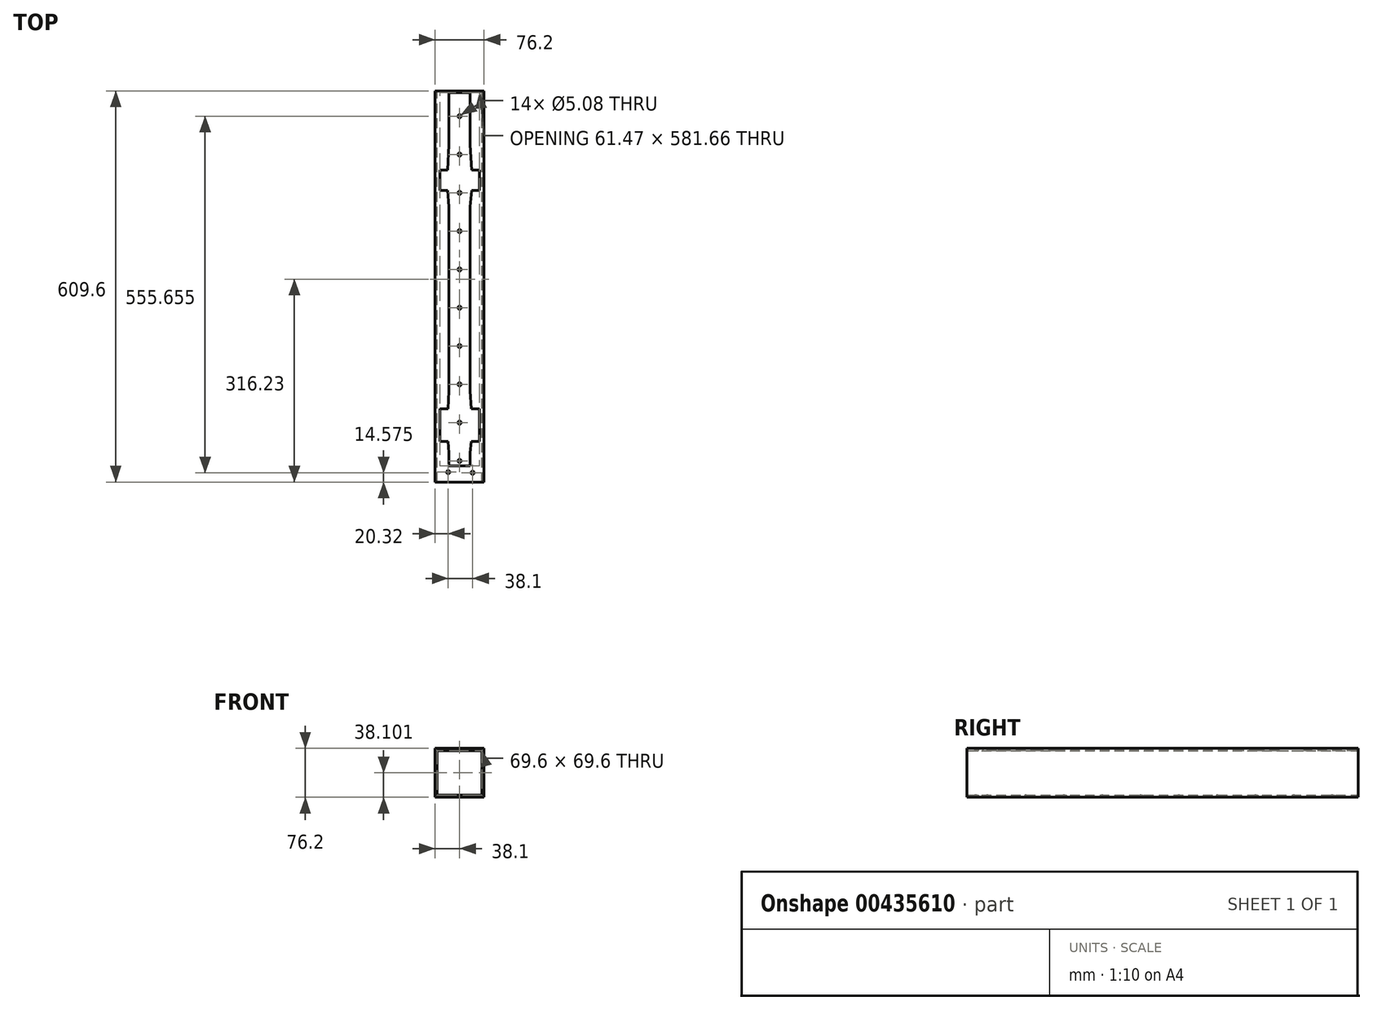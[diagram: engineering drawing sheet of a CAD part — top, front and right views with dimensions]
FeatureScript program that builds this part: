
annotation { "Feature Type Name" : "Feature", "Feature Type Description" : "" }
export const myFeature = defineFeature(function(context is Context, id is Id, definition is map)
    precondition{}
    {
        {
            var Q0;
            Q0=qCreatedBy(makeId("Front.planeOp"),FACE);
            var sketch = newSketch(context, id + "F0", { "sketchPlane" : qUnion([Q0])});
            skLineSegment(sketch, "E0.bottom", {"start": v(-13.17, 53.42) * mm, "end": v(56.43, 53.42) * mm});
            skLineSegment(sketch, "E0.top", {"start": v(-13.17, -16.18) * mm, "end": v(56.43, -16.18) * mm});
            skLineSegment(sketch, "E0.left", {"start": v(-13.17, 53.42) * mm, "end": v(-13.17, -16.18) * mm});
            skLineSegment(sketch, "E0.right", {"start": v(56.43, 53.42) * mm, "end": v(56.43, -16.18) * mm});
            skLineSegment(sketch, "E1.bottom", {"start": v(-16.47, 56.72) * mm, "end": v(59.73, 56.72) * mm});
            skLineSegment(sketch, "E1.top", {"start": v(-16.47, -19.48) * mm, "end": v(59.73, -19.48) * mm});
            skLineSegment(sketch, "E1.left", {"start": v(-16.47, 56.72) * mm, "end": v(-16.47, -19.48) * mm});
            skLineSegment(sketch, "E1.right", {"start": v(59.73, 56.72) * mm, "end": v(59.73, -19.48) * mm});
            skSolve(sketch);
        }
        {
            var Q0;
            Q0=makeQuery(id+"F0.imprint","IMPRINT",FACE,{"disambiguationData":[TD([[makeQuery(id+"F0.imprint","IMPRINT",EDGE,{"derivedFrom":sQuery(id+"F0.wireOp",EDGE,"E0.bottom")}),1.0]])]});
            extrude(context, id + "F1", {"entities" : qUnion([Q0]), "depth" : 609.6 * mm, "offsetDistance" : 25.4 * mm});
        }
        {
            var Q0;
            Q0=makeQuery(id+"F1.opExtrude","SWEPT_FACE",FACE,{"disambiguationData":[OSD([sQuery(id+"F0.wireOp",EDGE,"E1.bottom")])]});
            var sketch = newSketch(context, id + "F2", { "sketchPlane" : qUnion([Q0])});
            skLineSegment(sketch, "E2", {"start": v(5.12, -2.54) * mm, "end": v(38.14, -2.54) * mm});
            skLineSegment(sketch, "E3", {"start": v(38.14, -2.54) * mm, "end": v(38.14, -83.82) * mm});
            skLineSegment(sketch, "E4", {"start": v(5.12, -83.82) * mm, "end": v(5.12, -2.54) * mm});
            skLineSegment(sketch, "E5", {"start": v(38.14, -83.82) * mm, "end": v(40.43, -123.2) * mm});
            skLineSegment(sketch, "E6", {"start": v(40.43, -123.2) * mm, "end": v(52.36, -123.2) * mm});
            skLineSegment(sketch, "E7", {"start": v(52.36, -123.2) * mm, "end": v(52.36, -154.94) * mm});
            skLineSegment(sketch, "E8", {"start": v(52.36, -154.94) * mm, "end": v(40.43, -154.94) * mm});
            skLineSegment(sketch, "E9", {"start": v(-9.1, -123.2) * mm, "end": v(-9.1, -154.94) * mm});
            skLineSegment(sketch, "E10", {"start": v(-9.1, -154.94) * mm, "end": v(2.83, -154.94) * mm});
            skLineSegment(sketch, "E11", {"start": v(-9.1, -123.2) * mm, "end": v(2.83, -123.2) * mm});
            skLineSegment(sketch, "E12", {"start": v(2.83, -123.2) * mm, "end": v(5.12, -83.82) * mm});
            skLineSegment(sketch, "E13", {"start": v(2.83, -154.94) * mm, "end": v(5.12, -180.34) * mm});
            skLineSegment(sketch, "E14", {"start": v(40.43, -154.94) * mm, "end": v(38.14, -180.34) * mm});
            skLineSegment(sketch, "E15", {"start": v(5.12, -180.34) * mm, "end": v(5.12, -467.36) * mm});
            skLineSegment(sketch, "E16", {"start": v(38.14, -180.34) * mm, "end": v(38.14, -467.36) * mm});
            skLineSegment(sketch, "E17", {"start": v(5.12, -467.36) * mm, "end": v(3.6, -495.3) * mm});
            skLineSegment(sketch, "E18", {"start": v(3.6, -495.3) * mm, "end": v(-9.1, -495.3) * mm});
            skLineSegment(sketch, "E19", {"start": v(-9.1, -495.3) * mm, "end": v(-9.1, -546.1) * mm});
            skLineSegment(sketch, "E20", {"start": v(-9.1, -546.1) * mm, "end": v(3.6, -546.1) * mm});
            skLineSegment(sketch, "E21", {"start": v(3.6, -546.1) * mm, "end": v(5.25, -563.88) * mm});
            skLineSegment(sketch, "E22", {"start": v(5.25, -563.88) * mm, "end": v(5.25, -584.2) * mm});
            skLineSegment(sketch, "E23", {"start": v(5.25, -584.2) * mm, "end": v(38.27, -584.2) * mm});
            skLineSegment(sketch, "E24", {"start": v(38.27, -584.2) * mm, "end": v(38.27, -563.88) * mm});
            skLineSegment(sketch, "E25", {"start": v(38.27, -563.88) * mm, "end": v(39.66, -546.1) * mm});
            skLineSegment(sketch, "E26", {"start": v(39.66, -546.1) * mm, "end": v(52.36, -546.1) * mm});
            skLineSegment(sketch, "E27", {"start": v(52.36, -546.1) * mm, "end": v(52.36, -495.3) * mm});
            skLineSegment(sketch, "E28", {"start": v(52.36, -495.3) * mm, "end": v(39.66, -495.3) * mm});
            skLineSegment(sketch, "E29", {"start": v(39.66, -495.3) * mm, "end": v(38.14, -467.36) * mm});
            skSolve(sketch);
        }
        {
            var Q0;
            Q0=makeQuery(id+"F2.imprint","IMPRINT",FACE,{"disambiguationData":[TD([[makeQuery(id+"F2.imprint","IMPRINT",EDGE,{"derivedFrom":sQuery(id+"F2.wireOp",EDGE,"E2")}),-1.0]])]});
            extrude(context, id + "F3", {"entities" : qUnion([Q0]), "operationType" : NewBodyOperationType.REMOVE, "oppositeDirection" : true, "depth" : 25.4 * mm, "offsetDistance" : 25.4 * mm});
        }
        {
            var Q0;
            Q0=makeQuery(id+"F1.opExtrude","SWEPT_FACE",FACE,{"disambiguationData":[OSD([sQuery(id+"F0.wireOp",EDGE,"E1.top")])]});
            var sketch = newSketch(context, id + "F4", { "sketchPlane" : qUnion([Q0])});
            skPoint(sketch, "E30", {"position": v(21.63, 576.58) * mm});
            skPoint(sketch, "E31", {"position": v(21.63, 516.9) * mm});
            skPoint(sketch, "E32", {"position": v(21.63, 457.2) * mm});
            skPoint(sketch, "E33", {"position": v(21.63, 397.5) * mm});
            skPoint(sketch, "E34", {"position": v(21.63, 337.82) * mm});
            skPoint(sketch, "E35", {"position": v(21.63, 278.13) * mm});
            skPoint(sketch, "E36", {"position": v(21.63, 218.44) * mm});
            skPoint(sketch, "E37", {"position": v(21.63, 158.75) * mm});
            skPoint(sketch, "E38", {"position": v(21.63, 99.06) * mm});
            skPoint(sketch, "E39", {"position": v(21.63, 39.37) * mm});
            skPoint(sketch, "E40", {"position": v(3.85, 594.04) * mm});
            skPoint(sketch, "E41", {"position": v(41.95, 595.03) * mm});
            skSolve(sketch);
        }
        {
            var Q0;
            Q0=sQuery(id+"F4.wireOp",VERTEX,"E30");
            var Q1;
            Q1=sQuery(id+"F4.wireOp",VERTEX,"E31");
            var Q2;
            Q2=sQuery(id+"F4.wireOp",VERTEX,"E32");
            var Q3;
            Q3=sQuery(id+"F4.wireOp",VERTEX,"E33");
            var Q4;
            Q4=sQuery(id+"F4.wireOp",VERTEX,"E34");
            var Q5;
            Q5=sQuery(id+"F4.wireOp",VERTEX,"E35");
            var Q6;
            Q6=sQuery(id+"F4.wireOp",VERTEX,"E36");
            var Q7;
            Q7=sQuery(id+"F4.wireOp",VERTEX,"E37");
            var Q8;
            Q8=sQuery(id+"F4.wireOp",VERTEX,"E38");
            var Q9;
            Q9=sQuery(id+"F4.wireOp",VERTEX,"E39");
            var Q10;
            Q10=sQuery(id+"F4.wireOp",VERTEX,"E40");
            var Q11;
            Q11=sQuery(id+"F4.wireOp",VERTEX,"E41");
            var Q12;
            Q12=makeQuery(id+"F1.opExtrude","SWEPT_BODY",BODY,{"disambiguationData":[OSD([sQuery(id+"F0.wireOp",EDGE,"E0.bottom"),sQuery(id+"F0.wireOp",EDGE,"E0.top"),sQuery(id+"F0.wireOp",EDGE,"E0.left"),sQuery(id+"F0.wireOp",EDGE,"E0.right"),sQuery(id+"F0.wireOp",EDGE,"E1.bottom"),sQuery(id+"F0.wireOp",EDGE,"E1.top"),sQuery(id+"F0.wireOp",EDGE,"E1.left"),sQuery(id+"F0.wireOp",EDGE,"E1.right")])]});
            hole(context, id + "F5", {"style" : HoleStyle.SIMPLE, "endStyle" : HoleEndStyle.THROUGH, "holeDiameter" : 5.08 * mm, "majorDiameter" : 6.35 * mm, "isTappedThrough" : true, "tappedDepth" : 12.7 * mm, "tapClearance" : 3, "locations" : qUnion([Q0, Q1, Q2, Q3, Q4, Q5, Q6, Q7, Q8, Q9, Q10, Q11]), "scope" : qUnion([Q12])});
        }
    });
